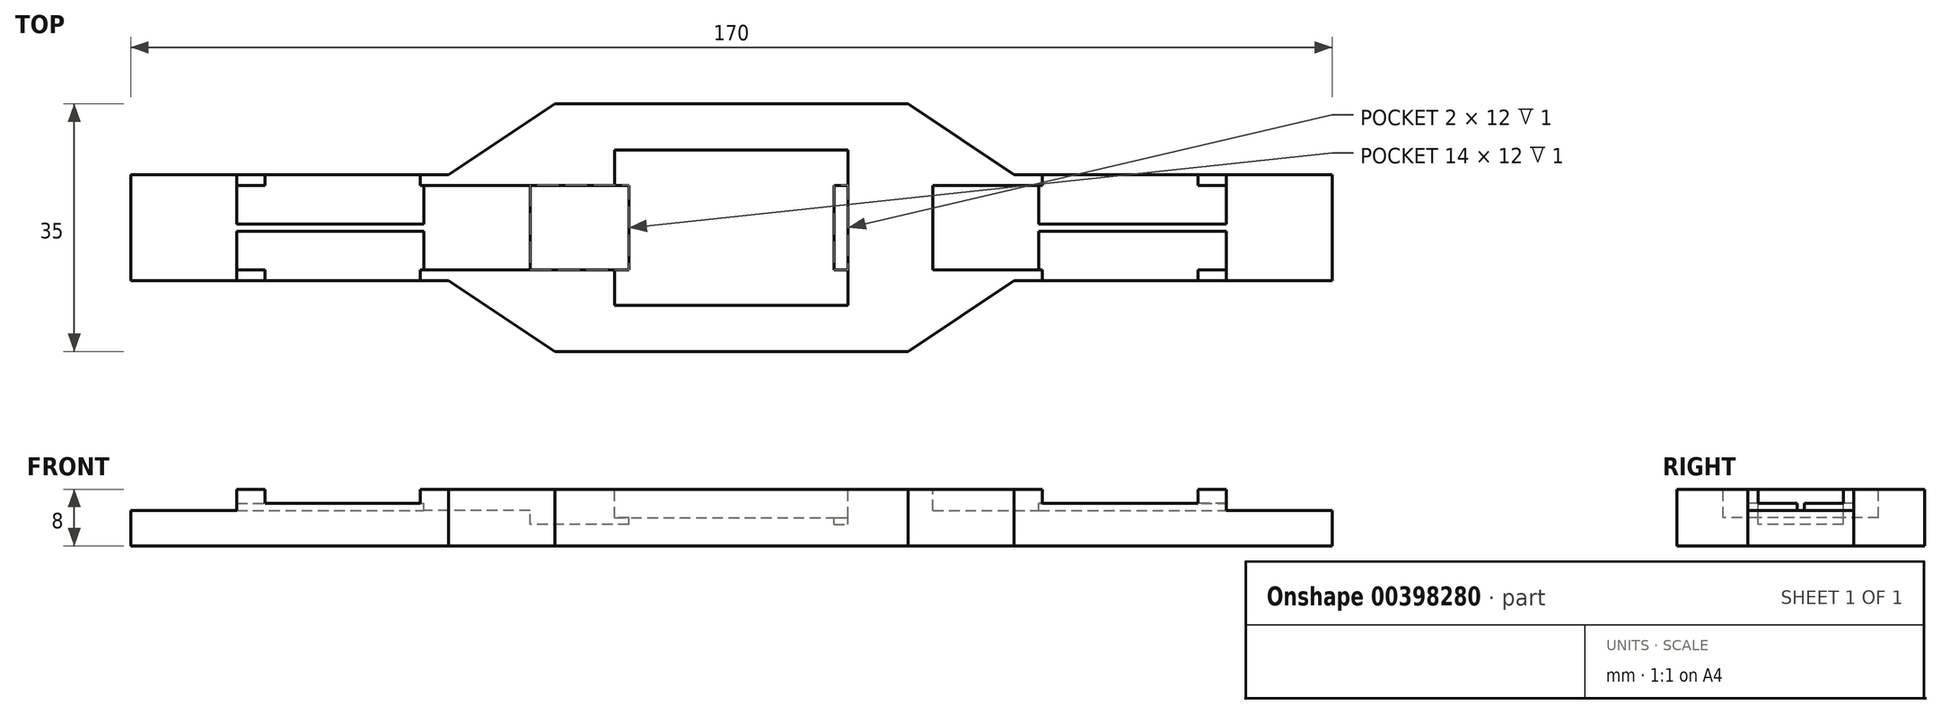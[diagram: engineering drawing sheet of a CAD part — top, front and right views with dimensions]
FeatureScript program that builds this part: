
annotation { "Feature Type Name" : "Feature", "Feature Type Description" : "" }
export const myFeature = defineFeature(function(context is Context, id is Id, definition is map)
    precondition{}
    {
        {
            var Q0;
            Q0=qCreatedBy(makeId("Top.planeOp"),FACE);
            var sketch = newSketch(context, id + "F0", { "sketchPlane" : qUnion([Q0])});
            skLineSegment(sketch, "E0", {"start": v(-25, -17.5) * mm, "end": v(25, -17.5) * mm});
            skLineSegment(sketch, "E1", {"start": v(25, -17.5) * mm, "end": v(40, -7.5) * mm});
            skLineSegment(sketch, "E2", {"start": v(40, -7.5) * mm, "end": v(85, -7.5) * mm});
            skLineSegment(sketch, "E3", {"start": v(85, -7.5) * mm, "end": v(85, 7.5) * mm});
            skLineSegment(sketch, "E4", {"start": v(40, 7.5) * mm, "end": v(25, 17.5) * mm});
            skLineSegment(sketch, "E5", {"start": v(-25, 17.5) * mm, "end": v(25, 17.5) * mm});
            skLineSegment(sketch, "E6", {"start": v(40, 7.5) * mm, "end": v(85, 7.5) * mm});
            skLineSegment(sketch, "E7", {"start": v(-25, 17.5) * mm, "end": v(-40, 7.5) * mm});
            skLineSegment(sketch, "E8", {"start": v(-40, 7.5) * mm, "end": v(-85, 7.5) * mm});
            skLineSegment(sketch, "E9", {"start": v(-85, -7.5) * mm, "end": v(-40, -7.5) * mm});
            skLineSegment(sketch, "E10", {"start": v(-25, -17.5) * mm, "end": v(-40, -7.5) * mm});
            skLineSegment(sketch, "E11", {"start": v(-85, 7.5) * mm, "end": v(-85, -7.5) * mm});
            skSolve(sketch);
        }
        {
            var Q0;
            Q0 = qSketchRegion(id + "F0", true);
            extrude(context, id + "F1", {"entities" : qUnion([Q0]), "depth" : 8 * mm});
        }
        {
            var Q0;
            Q0=makeQuery(id+"F1.opExtrude","CAP_FACE",FACE,{"disambiguationData":[OSD([sQuery(id+"F0.wireOp",EDGE,"E0"),sQuery(id+"F0.wireOp",EDGE,"E1"),sQuery(id+"F0.wireOp",EDGE,"E2"),sQuery(id+"F0.wireOp",EDGE,"E3"),sQuery(id+"F0.wireOp",EDGE,"E4"),sQuery(id+"F0.wireOp",EDGE,"E5"),sQuery(id+"F0.wireOp",EDGE,"E6"),sQuery(id+"F0.wireOp",EDGE,"E7"),sQuery(id+"F0.wireOp",EDGE,"E8"),sQuery(id+"F0.wireOp",EDGE,"E9"),sQuery(id+"F0.wireOp",EDGE,"E10"),sQuery(id+"F0.wireOp",EDGE,"E11")])],"isStart":false});
            var sketch = newSketch(context, id + "F2", { "sketchPlane" : qUnion([Q0])});
            skLineSegment(sketch, "E12.bottom", {"start": v(-16.5, 11) * mm, "end": v(16.5, 11) * mm});
            skLineSegment(sketch, "E12.top", {"start": v(-16.5, -11) * mm, "end": v(16.5, -11) * mm});
            skLineSegment(sketch, "E12.left", {"start": v(-16.5, 11) * mm, "end": v(-16.5, -11) * mm});
            skLineSegment(sketch, "E12.right", {"start": v(16.5, 11) * mm, "end": v(16.5, -11) * mm});
            skLineSegment(sketch, "E13.bottom", {"start": v(-14.5, 6) * mm, "end": v(-28.5, 6) * mm});
            skLineSegment(sketch, "E13.top", {"start": v(-14.5, -6) * mm, "end": v(-28.5, -6) * mm});
            skLineSegment(sketch, "E13.left", {"start": v(-14.5, 6) * mm, "end": v(-14.5, -6) * mm});
            skLineSegment(sketch, "E13.right", {"start": v(-28.5, 6) * mm, "end": v(-28.5, -6) * mm});
            skLineSegment(sketch, "E14.bottom", {"start": v(-28.5, 6) * mm, "end": v(-43.5, 6) * mm});
            skLineSegment(sketch, "E14.top", {"start": v(-28.5, -6) * mm, "end": v(-43.5, -6) * mm});
            skLineSegment(sketch, "E14.right", {"start": v(-43.5, 6) * mm, "end": v(-43.5, -6) * mm});
            skLineSegment(sketch, "E15.bottom", {"start": v(-85, 6) * mm, "end": v(-43.5, 6) * mm});
            skLineSegment(sketch, "E15.top", {"start": v(-85, -6) * mm, "end": v(-43.5, -6) * mm});
            skLineSegment(sketch, "E15.left", {"start": v(-85, 6) * mm, "end": v(-85, -6) * mm});
            skLineSegment(sketch, "E16.bottom", {"start": v(85, 6) * mm, "end": v(43.5, 6) * mm});
            skLineSegment(sketch, "E16.top", {"start": v(85, -6) * mm, "end": v(43.5, -6) * mm});
            skLineSegment(sketch, "E16.left", {"start": v(85, 6) * mm, "end": v(85, -6) * mm});
            skLineSegment(sketch, "E16.right", {"start": v(43.5, 6) * mm, "end": v(43.5, -6) * mm});
            skLineSegment(sketch, "E17.bottom", {"start": v(14.5, 6) * mm, "end": v(28.5, 6) * mm});
            skLineSegment(sketch, "E17.top", {"start": v(14.5, -6) * mm, "end": v(28.5, -6) * mm});
            skLineSegment(sketch, "E17.left", {"start": v(14.5, 6) * mm, "end": v(14.5, -6) * mm});
            skLineSegment(sketch, "E17.right", {"start": v(28.5, 6) * mm, "end": v(28.5, -6) * mm});
            skLineSegment(sketch, "E18.bottom", {"start": v(28.5, -6) * mm, "end": v(43.5, -6) * mm});
            skLineSegment(sketch, "E18.top", {"start": v(28.5, 6) * mm, "end": v(43.5, 6) * mm});
            skLineSegment(sketch, "E18.left", {"start": v(28.5, -6) * mm, "end": v(28.5, 6) * mm});
            skLineSegment(sketch, "E18.right", {"start": v(43.5, -6) * mm, "end": v(43.5, 6) * mm});
            skLineSegment(sketch, "E19.bottom", {"start": v(-85, 7.5) * mm, "end": v(-70, 7.5) * mm});
            skLineSegment(sketch, "E19.top", {"start": v(-85, -7.5) * mm, "end": v(-70, -7.5) * mm});
            skLineSegment(sketch, "E19.left", {"start": v(-85, 7.5) * mm, "end": v(-85, -7.5) * mm});
            skLineSegment(sketch, "E19.right", {"start": v(-70, 7.5) * mm, "end": v(-70, -7.5) * mm});
            skLineSegment(sketch, "E20.bottom", {"start": v(-66, 7.5) * mm, "end": v(-44, 7.5) * mm});
            skLineSegment(sketch, "E20.top", {"start": v(-66, -7.5) * mm, "end": v(-44, -7.5) * mm});
            skLineSegment(sketch, "E20.left", {"start": v(-66, 7.5) * mm, "end": v(-66, -7.5) * mm});
            skLineSegment(sketch, "E20.right", {"start": v(-44, 7.5) * mm, "end": v(-44, -7.5) * mm});
            skLineSegment(sketch, "E21.bottom", {"start": v(85, 7.5) * mm, "end": v(70, 7.5) * mm});
            skLineSegment(sketch, "E21.top", {"start": v(85, -7.5) * mm, "end": v(70, -7.5) * mm});
            skLineSegment(sketch, "E21.left", {"start": v(85, 7.5) * mm, "end": v(85, -7.5) * mm});
            skLineSegment(sketch, "E21.right", {"start": v(70, 7.5) * mm, "end": v(70, -7.5) * mm});
            skLineSegment(sketch, "E22.bottom", {"start": v(44, 7.5) * mm, "end": v(66, 7.5) * mm});
            skLineSegment(sketch, "E22.top", {"start": v(44, -7.5) * mm, "end": v(66, -7.5) * mm});
            skLineSegment(sketch, "E22.left", {"start": v(44, 7.5) * mm, "end": v(44, -7.5) * mm});
            skLineSegment(sketch, "E22.right", {"start": v(66, 7.5) * mm, "end": v(66, -7.5) * mm});
            skSolve(sketch);
        }
        {
            var Q0;
            Q0=makeQuery(id+"F2.imprint","IMPRINT",FACE,{"disambiguationData":[TD([[makeQuery(id+"F2.imprint","IMPRINT",EDGE,{"derivedFrom":sQuery(id+"F2.wireOp",EDGE,"E15.bottom")}),-1.0]])]});
            var Q1;
            Q1=makeQuery(id+"F2.imprint","IMPRINT",FACE,{"disambiguationData":[TD([[makeQuery(id+"F2.imprint","IMPRINT",EDGE,{"derivedFrom":sQuery(id+"F2.wireOp",EDGE,"E16.bottom")}),1.0]])]});
            extrude(context, id + "F3", {"entities" : qUnion([Q0, Q1]), "operationType" : NewBodyOperationType.REMOVE, "oppositeDirection" : true, "depth" : 2 * mm});
        }
        {
            var Q0;
            Q0=makeQuery(id+"F2.imprint","IMPRINT",FACE,{"disambiguationData":[TD([[makeQuery(id+"F2.imprint","IMPRINT",EDGE,{"derivedFrom":sQuery(id+"F2.wireOp",EDGE,"E14.bottom")}),1.0]])]});
            var Q1;
            Q1=makeQuery(id+"F2.imprint","IMPRINT",FACE,{"disambiguationData":[TD([[makeQuery(id+"F2.imprint","IMPRINT",EDGE,{"derivedFrom":sQuery(id+"F2.wireOp",EDGE,"E18.bottom")}),1.0]])]});
            extrude(context, id + "F4", {"entities" : qUnion([Q0, Q1]), "operationType" : NewBodyOperationType.REMOVE, "oppositeDirection" : true, "depth" : 3 * mm});
        }
        {
            var Q0;
            {var subQ5=sQuery(id+"F2.wireOp",EDGE,"E13.right");Q0=makeQuery(id+"F2.imprint","IMPRINT",FACE,{"disambiguationData":[TD([[makeQuery(id+"F2.imprint","IMPRINT",EDGE,{"derivedFrom":subQ5}),1.0]])]});}
            var Q1;
            {var subQ5=sQuery(id+"F2.wireOp",EDGE,"E13.left");Q1=makeQuery(id+"F2.imprint","IMPRINT",FACE,{"disambiguationData":[TD([[makeQuery(id+"F2.imprint","IMPRINT",EDGE,{"derivedFrom":subQ5}),-1.0]])]});}
            var Q2;
            {var subQ5=sQuery(id+"F2.wireOp",EDGE,"E17.left");Q2=makeQuery(id+"F2.imprint","IMPRINT",FACE,{"disambiguationData":[TD([[makeQuery(id+"F2.imprint","IMPRINT",EDGE,{"derivedFrom":subQ5}),1.0]])]});}
            var Q3;
            {var subQ5=sQuery(id+"F2.wireOp",EDGE,"E18.left");Q3=makeQuery(id+"F2.imprint","IMPRINT",FACE,{"disambiguationData":[TD([[makeQuery(id+"F2.imprint","IMPRINT",EDGE,{"derivedFrom":subQ5}),1.0]])]});}
            extrude(context, id + "F5", {"entities" : qUnion([Q0, Q1, Q2, Q3]), "operationType" : NewBodyOperationType.REMOVE, "oppositeDirection" : true, "depth" : 5 * mm});
        }
        {
            var Q0;
            {var subQ10=sQuery(id+"F2.wireOp",EDGE,"E12.bottom");Q0=makeQuery(id+"F2.imprint","IMPRINT",FACE,{"disambiguationData":[TD([[makeQuery(id+"F2.imprint","IMPRINT",EDGE,{"derivedFrom":subQ10}),-1.0]])]});}
            extrude(context, id + "F6", {"entities" : qUnion([Q0]), "operationType" : NewBodyOperationType.REMOVE, "oppositeDirection" : true, "depth" : 4 * mm});
        }
        {
            var Q0;
            Q0=makeQuery(id+"F3.boolean.opBoolean","COPY",FACE,{"derivedFrom":makeQuery(id+"F3.opExtrude","CAP_FACE",FACE,{"disambiguationData":[OSD([sQuery(id+"F2.wireOp",EDGE,"E15.bottom"),sQuery(id+"F2.wireOp",EDGE,"E15.top"),sQuery(id+"F2.wireOp",EDGE,"E15.left"),sQuery(id+"F2.wireOp",EDGE,"E14.right")])],"isStart":false})});
            var sketch = newSketch(context, id + "F7", { "sketchPlane" : qUnion([Q0])});
            skLineSegment(sketch, "E23.bottom", {"start": v(-80, 0.5) * mm, "end": v(-43.5, 0.5) * mm});
            skLineSegment(sketch, "E23.top", {"start": v(-80, -0.5) * mm, "end": v(-43.5, -0.5) * mm});
            skLineSegment(sketch, "E23.left", {"start": v(-80, 0.5) * mm, "end": v(-80, -0.5) * mm});
            skLineSegment(sketch, "E23.right", {"start": v(-43.5, 0.5) * mm, "end": v(-43.5, -0.5) * mm});
            skSolve(sketch);
        }
        {
            var Q0;
            Q0=makeQuery(id+"F3.boolean.opBoolean","COPY",FACE,{"derivedFrom":makeQuery(id+"F3.opExtrude","CAP_FACE",FACE,{"disambiguationData":[OSD([sQuery(id+"F2.wireOp",EDGE,"E16.bottom"),sQuery(id+"F2.wireOp",EDGE,"E16.top"),sQuery(id+"F2.wireOp",EDGE,"E16.left"),sQuery(id+"F2.wireOp",EDGE,"E18.right")])],"isStart":false})});
            var sketch = newSketch(context, id + "F8", { "sketchPlane" : qUnion([Q0])});
            skLineSegment(sketch, "E24.bottom", {"start": v(43.5, 0.5) * mm, "end": v(80, 0.5) * mm});
            skLineSegment(sketch, "E24.top", {"start": v(43.5, -0.5) * mm, "end": v(80, -0.5) * mm});
            skLineSegment(sketch, "E24.left", {"start": v(43.5, 0.5) * mm, "end": v(43.5, -0.5) * mm});
            skLineSegment(sketch, "E24.right", {"start": v(80, 0.5) * mm, "end": v(80, -0.5) * mm});
            skSolve(sketch);
        }
        {
            var Q0;
            Q0=makeQuery(id+"F8.imprint","IMPRINT",FACE,{"disambiguationData":[TD([[makeQuery(id+"F8.imprint","IMPRINT",EDGE,{"derivedFrom":sQuery(id+"F8.wireOp",EDGE,"E24.bottom")}),-1.0]])]});
            var Q1;
            Q1=makeQuery(id+"F7.imprint","IMPRINT",FACE,{"disambiguationData":[TD([[makeQuery(id+"F7.imprint","IMPRINT",EDGE,{"derivedFrom":sQuery(id+"F7.wireOp",EDGE,"E23.bottom")}),-1.0]])]});
            extrude(context, id + "F9", {"entities" : qUnion([Q0, Q1]), "operationType" : NewBodyOperationType.REMOVE, "oppositeDirection" : true, "depth" : 1 * mm});
        }
        {
            var Q0;
            {var subQ5=sQuery(id+"F2.wireOp",EDGE,"E19.bottom");Q0=makeQuery(id+"F2.imprint","IMPRINT",FACE,{"disambiguationData":[TD([[makeQuery(id+"F2.imprint","IMPRINT",EDGE,{"derivedFrom":subQ5}),1.0]])]});}
            var Q1;
            {var subQ0=sQuery(id+"F2.wireOp",EDGE,"E19.left");var subQ1=sQuery(id+"F2.wireOp",EDGE,"E15.bottom");var subQ2=makeQuery(id+"F2.imprint","INTERSECT",VERTEX,{"derivedFrom":[subQ1,subQ0]});Q1=makeQuery(id+"F2.imprint","IMPRINT",FACE,{"disambiguationData":[TD([[makeQuery(id+"F2.imprint","IMPRINT",EDGE,{"disambiguationData":[TD([[subQ2,-1.0]])],"derivedFrom":subQ1}),-1.0]])]});}
            var Q2;
            {var subQ5=sQuery(id+"F2.wireOp",EDGE,"E19.top");Q2=makeQuery(id+"F2.imprint","IMPRINT",FACE,{"disambiguationData":[TD([[makeQuery(id+"F2.imprint","IMPRINT",EDGE,{"derivedFrom":subQ5}),1.0]])]});}
            extrude(context, id + "F10", {"entities" : qUnion([Q0, Q1, Q2]), "operationType" : NewBodyOperationType.REMOVE, "oppositeDirection" : true, "depth" : 3 * mm});
        }
        {
            var Q0;
            {var subQ5=sQuery(id+"F2.wireOp",EDGE,"E20.bottom");Q0=makeQuery(id+"F2.imprint","IMPRINT",FACE,{"disambiguationData":[TD([[makeQuery(id+"F2.imprint","IMPRINT",EDGE,{"derivedFrom":subQ5}),1.0]])]});}
            var Q1;
            {var subQ5=sQuery(id+"F2.wireOp",EDGE,"E20.top");Q1=makeQuery(id+"F2.imprint","IMPRINT",FACE,{"disambiguationData":[TD([[makeQuery(id+"F2.imprint","IMPRINT",EDGE,{"derivedFrom":subQ5}),1.0]])]});}
            extrude(context, id + "F11", {"entities" : qUnion([Q0, Q1]), "operationType" : NewBodyOperationType.REMOVE, "oppositeDirection" : true, "depth" : 2 * mm});
        }
        {
            var Q0;
            {var subQ5=sQuery(id+"F2.wireOp",EDGE,"E22.bottom");Q0=makeQuery(id+"F2.imprint","IMPRINT",FACE,{"disambiguationData":[TD([[makeQuery(id+"F2.imprint","IMPRINT",EDGE,{"derivedFrom":subQ5}),-1.0]])]});}
            var Q1;
            {var subQ5=sQuery(id+"F2.wireOp",EDGE,"E22.top");Q1=makeQuery(id+"F2.imprint","IMPRINT",FACE,{"disambiguationData":[TD([[makeQuery(id+"F2.imprint","IMPRINT",EDGE,{"derivedFrom":subQ5}),1.0]])]});}
            extrude(context, id + "F12", {"entities" : qUnion([Q0, Q1]), "operationType" : NewBodyOperationType.REMOVE, "oppositeDirection" : true, "depth" : 2 * mm});
        }
        {
            var Q0;
            {var subQ5=sQuery(id+"F2.wireOp",EDGE,"E21.bottom");Q0=makeQuery(id+"F2.imprint","IMPRINT",FACE,{"disambiguationData":[TD([[makeQuery(id+"F2.imprint","IMPRINT",EDGE,{"derivedFrom":subQ5}),-1.0]])]});}
            var Q1;
            {var subQ5=sQuery(id+"F2.wireOp",EDGE,"E21.top");Q1=makeQuery(id+"F2.imprint","IMPRINT",FACE,{"disambiguationData":[TD([[makeQuery(id+"F2.imprint","IMPRINT",EDGE,{"derivedFrom":subQ5}),1.0]])]});}
            var Q2;
            {var subQ0=sQuery(id+"F2.wireOp",EDGE,"E21.left");var subQ1=sQuery(id+"F2.wireOp",EDGE,"E16.bottom");var subQ2=makeQuery(id+"F2.imprint","INTERSECT",VERTEX,{"derivedFrom":[subQ1,subQ0]});Q2=makeQuery(id+"F2.imprint","IMPRINT",FACE,{"disambiguationData":[TD([[makeQuery(id+"F2.imprint","IMPRINT",EDGE,{"disambiguationData":[TD([[subQ2,-1.0]])],"derivedFrom":subQ1}),1.0]])]});}
            extrude(context, id + "F13", {"entities" : qUnion([Q0, Q1, Q2]), "operationType" : NewBodyOperationType.REMOVE, "oppositeDirection" : true, "depth" : 3 * mm});
        }
    });
